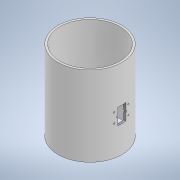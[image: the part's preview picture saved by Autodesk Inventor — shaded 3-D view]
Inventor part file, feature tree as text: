
AUTODESK INVENTOR PART (.ipt)
format: ipt  version: 2022 (Build 260153000, 153)  size: 173,568 bytes
history: native  units: mm
features: extrude x5, sketch x5, plane x3
ambient origin geometry x8: Origin, YZ Plane, XZ Plane, XY Plane, X Axis, Y Axis, Z Axis, Center Point
bodies: Solid1 (feature_tree)
feature tree (13):
  extrude  "Extrusion1"  Depth=40.0mm
  plane  "Work Plane3"
  extrude  "Extrusion9"  [1 undecoded]
  extrude  "Extrusion10"  Depth=5.0mm
  plane  "Work Plane4"
  extrude  "Extrusion11"  Depth=10.0mm TaperAngle=0.0deg
  plane  "Work Plane5"
  extrude  "Extrusion12"  Depth=6.0mm
  sketch  "Sketch1"  dims[d0=37.47mm d1=40.0mm]
  sketch  "Sketch8"  dims[d2=50.0mm d3=0.0mm d34=-21.88mm]
  sketch  "Sketch9"  dims[d35=3.0mm d36=5.0mm]
  sketch  "Sketch11"  dims[d37=2.5mm d40=10.0mm d41=0.0mm]
  sketch  "Sketch12"  dims[d42=3.0mm d43=6.0mm d44=3.0mm d46=18.0mm d47=1.0mm d48=0.0mm d54=0.75mm d55=2.0mm d56=2.0mm d57=1.0mm d58=0.0mm d59=0.75mm d60=2.0mm d61=2.0mm d62=1.0mm d63=0.0mm d6=0.5mm d7=0.872665mm d8=0.5mm d9=0.872665mm d49=0.5mm d50=0.872665mm]
note: 1 required parameter value undecoded (feature->parameter linkage not recoverable at this tier; creation-order binding heuristic only, values carry confidence <= 0.55)
